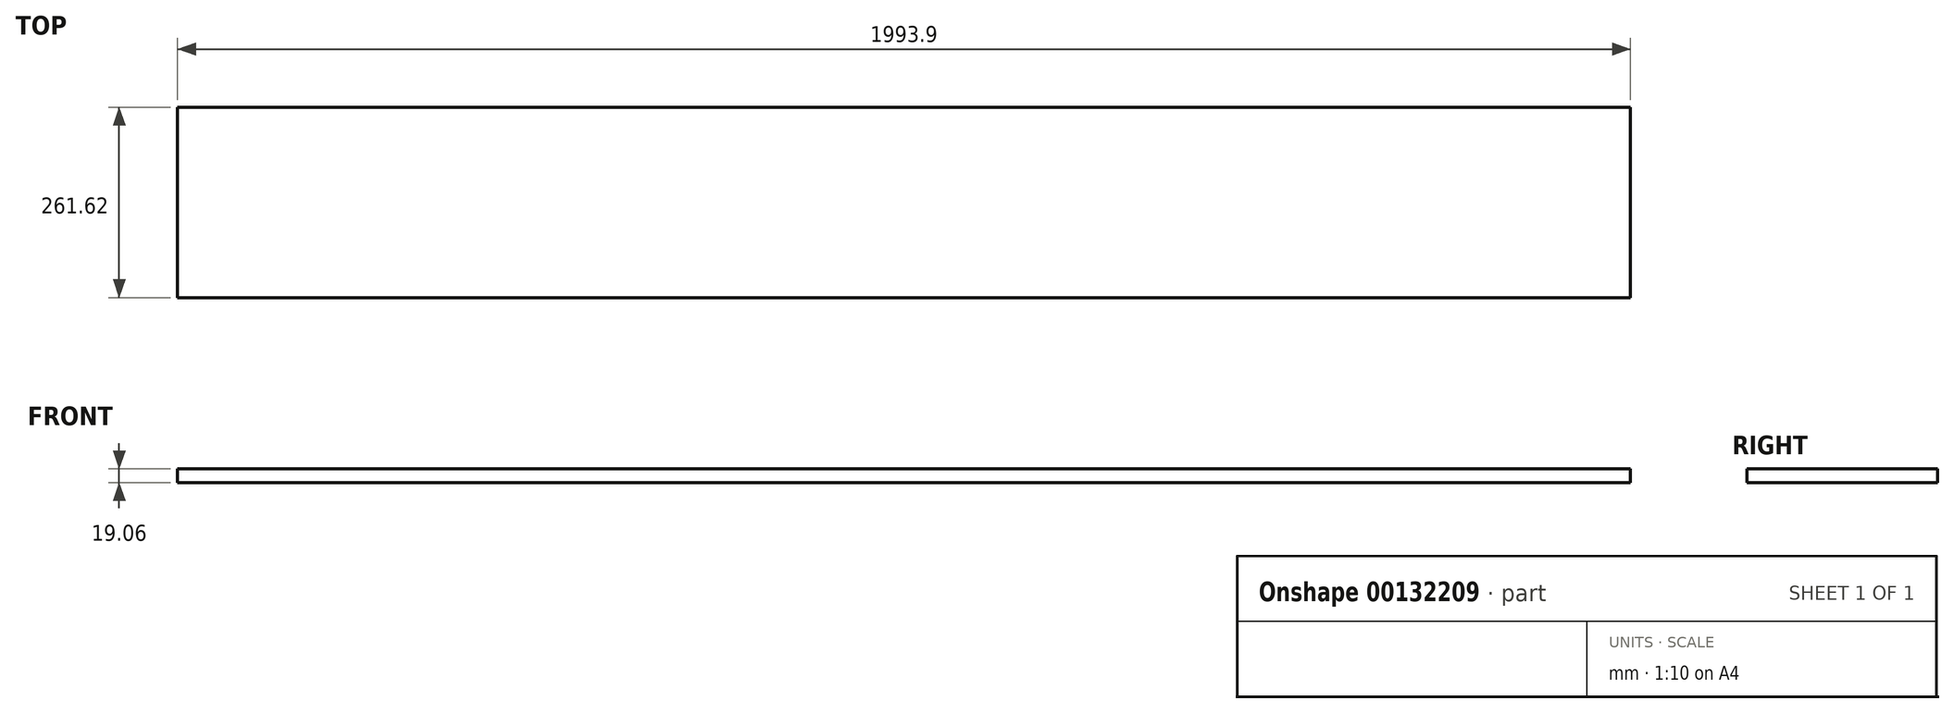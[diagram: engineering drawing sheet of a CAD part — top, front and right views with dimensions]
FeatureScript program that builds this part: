
annotation { "Feature Type Name" : "Feature", "Feature Type Description" : "" }
export const myFeature = defineFeature(function(context is Context, id is Id, definition is map)
    precondition{}
    {
        {
            var Q0;
            Q0=qCreatedBy(makeId("Top.planeOp"),FACE);
            var sketch = newSketch(context, id + "F0", { "sketchPlane" : qUnion([Q0])});
            skLineSegment(sketch, "E0.bottom", {"start": v(996.95, 130.81) * mm, "end": v(-996.95, 130.81) * mm});
            skLineSegment(sketch, "E0.top", {"start": v(996.95, -130.81) * mm, "end": v(-996.95, -130.81) * mm});
            skLineSegment(sketch, "E0.left", {"start": v(996.95, 130.81) * mm, "end": v(996.95, -130.81) * mm});
            skLineSegment(sketch, "E0.right", {"start": v(-996.95, 130.81) * mm, "end": v(-996.95, -130.81) * mm});
            skPoint(sketch, "E0.middle", {"position": v(0, 0) * mm});
            skSolve(sketch);
        }
        {
            var Q0;
            Q0=makeQuery(id+"F0.imprint","IMPRINT",FACE,{"disambiguationData":[TD([[makeQuery(id+"F0.imprint","IMPRINT",EDGE,{"derivedFrom":sQuery(id+"F0.wireOp",EDGE,"E0.bottom")}),1.0]])]});
            extrude(context, id + "F1", {"entities" : qUnion([Q0]), "endBound" : BoundingType.SYMMETRIC, "depth" : 19.05 * mm});
        }
    });
